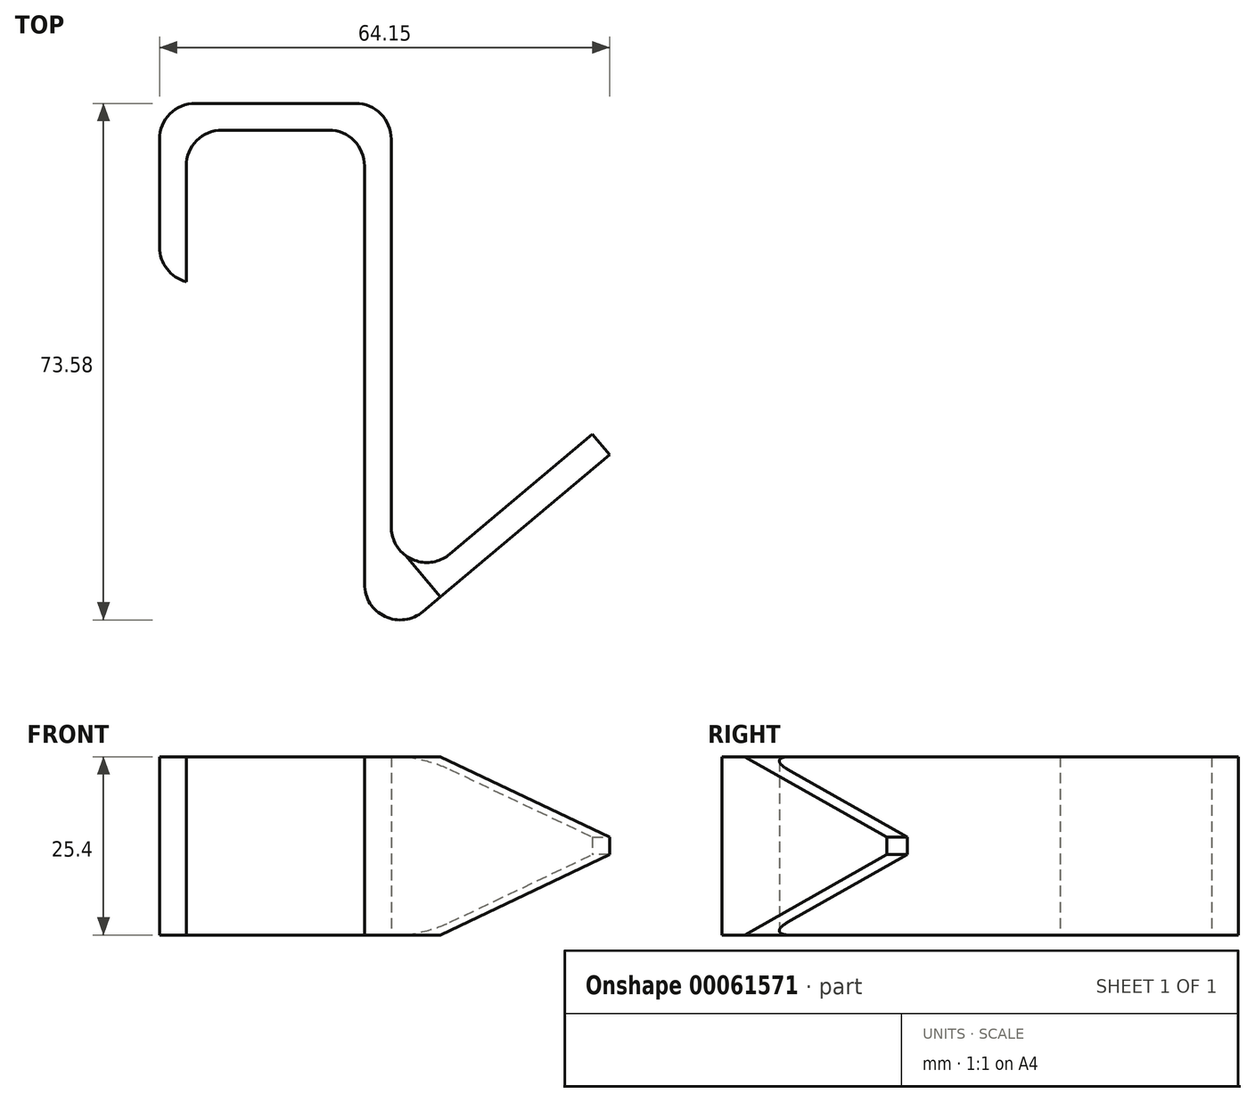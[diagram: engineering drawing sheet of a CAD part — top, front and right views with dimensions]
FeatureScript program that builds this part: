
annotation { "Feature Type Name" : "Feature", "Feature Type Description" : "" }
export const myFeature = defineFeature(function(context is Context, id is Id, definition is map)
    precondition{}
    {
        {
            var Q0;
            Q0=qCreatedBy(makeId("Top.planeOp"),FACE);
            var sketch = newSketch(context, id + "F0", { "sketchPlane" : qUnion([Q0])});
            skLineSegment(sketch, "E0", {"start": v(0, 0) * mm, "end": v(0, -25.4) * mm});
            skLineSegment(sketch, "E1", {"start": v(0, 0) * mm, "end": v(33.02, 0) * mm});
            skLineSegment(sketch, "E2", {"start": v(3.81, -3.8) * mm, "end": v(29.21, -3.8) * mm});
            skLineSegment(sketch, "E3", {"start": v(3.81, -3.8) * mm, "end": v(3.81, -25.4) * mm});
            skLineSegment(sketch, "E4", {"start": v(0, -25.4) * mm, "end": v(3.81, -25.4) * mm});
            skLineSegment(sketch, "E5", {"start": v(33.02, 0) * mm, "end": v(33.02, -71.23) * mm});
            skLineSegment(sketch, "E6", {"start": v(33.02, -76.2) * mm, "end": v(29.21, -76.2) * mm});
            skLineSegment(sketch, "E7", {"start": v(29.21, -76.2) * mm, "end": v(29.21, -3.8) * mm});
            skLineSegment(sketch, "E8", {"start": v(33.02, -76.2) * mm, "end": v(64.15, -50.08) * mm});
            skLineSegment(sketch, "E9", {"start": v(64.15, -50.08) * mm, "end": v(61.7, -47.16) * mm});
            skLineSegment(sketch, "E10", {"start": v(61.7, -47.16) * mm, "end": v(33.02, -71.23) * mm});
            skPoint(sketch, "E11.orphan", {"position": v(29.21, 0) * mm});
            skLineSegment(sketch, "E12", {"start": v(33.02, -71.23) * mm, "end": v(33.02, -76.2) * mm});
            skSolve(sketch);
        }
        {
            var Q0;
            Q0=makeQuery(id+"F0.imprint","IMPRINT",FACE,{"disambiguationData":[TD([[makeQuery(id+"F0.imprint","IMPRINT",EDGE,{"derivedFrom":sQuery(id+"F0.wireOp",EDGE,"E0")}),1.0]])]});
            var Q1;
            Q1=makeQuery(id+"F0.imprint","IMPRINT",FACE,{"disambiguationData":[TD([[makeQuery(id+"F0.imprint","IMPRINT",EDGE,{"derivedFrom":sQuery(id+"F0.wireOp",EDGE,"E8")}),1.0]])]});
            extrude(context, id + "F1", {"entities" : qUnion([Q0, Q1]), "depth" : 25.4 * mm});
        }
        {
            var Q0;
            Q0=makeQuery(id+"F1.opExtrude","SWEPT_EDGE",EDGE,{"disambiguationData":[OSD([sQuery(id+"F0.wireOp",EDGE,"E1"),sQuery(id+"F0.wireOp",EDGE,"E5")])]});
            var Q1;
            Q1=makeQuery(id+"F1.opExtrude","SWEPT_EDGE",EDGE,{"disambiguationData":[OSD([sQuery(id+"F0.wireOp",EDGE,"E0"),sQuery(id+"F0.wireOp",EDGE,"E1")])]});
            var Q2;
            Q2=makeQuery(id+"F1.opExtrude","SWEPT_EDGE",EDGE,{"disambiguationData":[OSD([sQuery(id+"F0.wireOp",EDGE,"E0"),sQuery(id+"F0.wireOp",EDGE,"E4")])]});
            var Q3;
            Q3=makeQuery(id+"F1.opExtrude","SWEPT_EDGE",EDGE,{"disambiguationData":[OSD([sQuery(id+"F0.wireOp",EDGE,"E2"),sQuery(id+"F0.wireOp",EDGE,"E3")])]});
            var Q4;
            Q4=makeQuery(id+"F1.opExtrude","SWEPT_EDGE",EDGE,{"disambiguationData":[OSD([sQuery(id+"F0.wireOp",EDGE,"E2"),sQuery(id+"F0.wireOp",EDGE,"E7")])]});
            var Q5;
            Q5=makeQuery(id+"F1.opExtrude","SWEPT_EDGE",EDGE,{"disambiguationData":[OSD([sQuery(id+"F0.wireOp",EDGE,"E5"),sQuery(id+"F0.wireOp",EDGE,"E10"),sQuery(id+"F0.wireOp",EDGE,"E12")])]});
            fillet(context, id + "F2", {"entities" : qUnion([Q0, Q1, Q2, Q3, Q4, Q5]), "radius" : 5.08 * mm, "tangentPropagation" : true, "allowEdgeOverflow" : false});
        }
        {
            var Q0;
            Q0=makeQuery(id+"F1.opExtrude","CAP_EDGE",EDGE,{"disambiguationData":[OSD([sQuery(id+"F0.wireOp",EDGE,"E9")])],"isStart":false});
            var Q1;
            Q1=makeQuery(id+"F1.opExtrude","CAP_EDGE",EDGE,{"disambiguationData":[OSD([sQuery(id+"F0.wireOp",EDGE,"E9")])],"isStart":true});
            chamfer(context, id + "F3", {"entities" : qUnion([Q0, Q1]), "chamferType" : ChamferType.OFFSET_ANGLE, "width" : 31.5 * mm, "oppositeDirection" : false, "angle" : 20 * degree, "tangentPropagation" : true});
        }
        {
            var Q0;
            Q0=makeQuery(id+"F1.opExtrude","SWEPT_EDGE",EDGE,{"disambiguationData":[OSD([sQuery(id+"F0.wireOp",EDGE,"E6"),sQuery(id+"F0.wireOp",EDGE,"E7")])]});
            fillet(context, id + "F4", {"entities" : qUnion([Q0]), "radius" : 5.08 * mm, "tangentPropagation" : true, "allowEdgeOverflow" : false});
        }
        {
            var Q0;
            Q0=makeQuery(id+"F4.opFillet","BLEND_EDGE",EDGE,{"blendedFrom":[makeQuery(id+"F1.opExtrude","SWEPT_EDGE",EDGE,{"disambiguationData":[OSD([sQuery(id+"F0.wireOp",EDGE,"E6"),sQuery(id+"F0.wireOp",EDGE,"E7")])]}),makeQuery(id+"F1.opExtrude","SWEPT_FACE",FACE,{"disambiguationData":[OSD([sQuery(id+"F0.wireOp",EDGE,"E8")])]})],"blendedInto":[makeQuery(id+"F1.opExtrude","SWEPT_FACE",FACE,{"disambiguationData":[OSD([sQuery(id+"F0.wireOp",EDGE,"E8")])]})]});
            fillet(context, id + "F5", {"entities" : qUnion([Q0]), "radius" : 5.08 * mm, "tangentPropagation" : true, "allowEdgeOverflow" : false});
        }
    });
